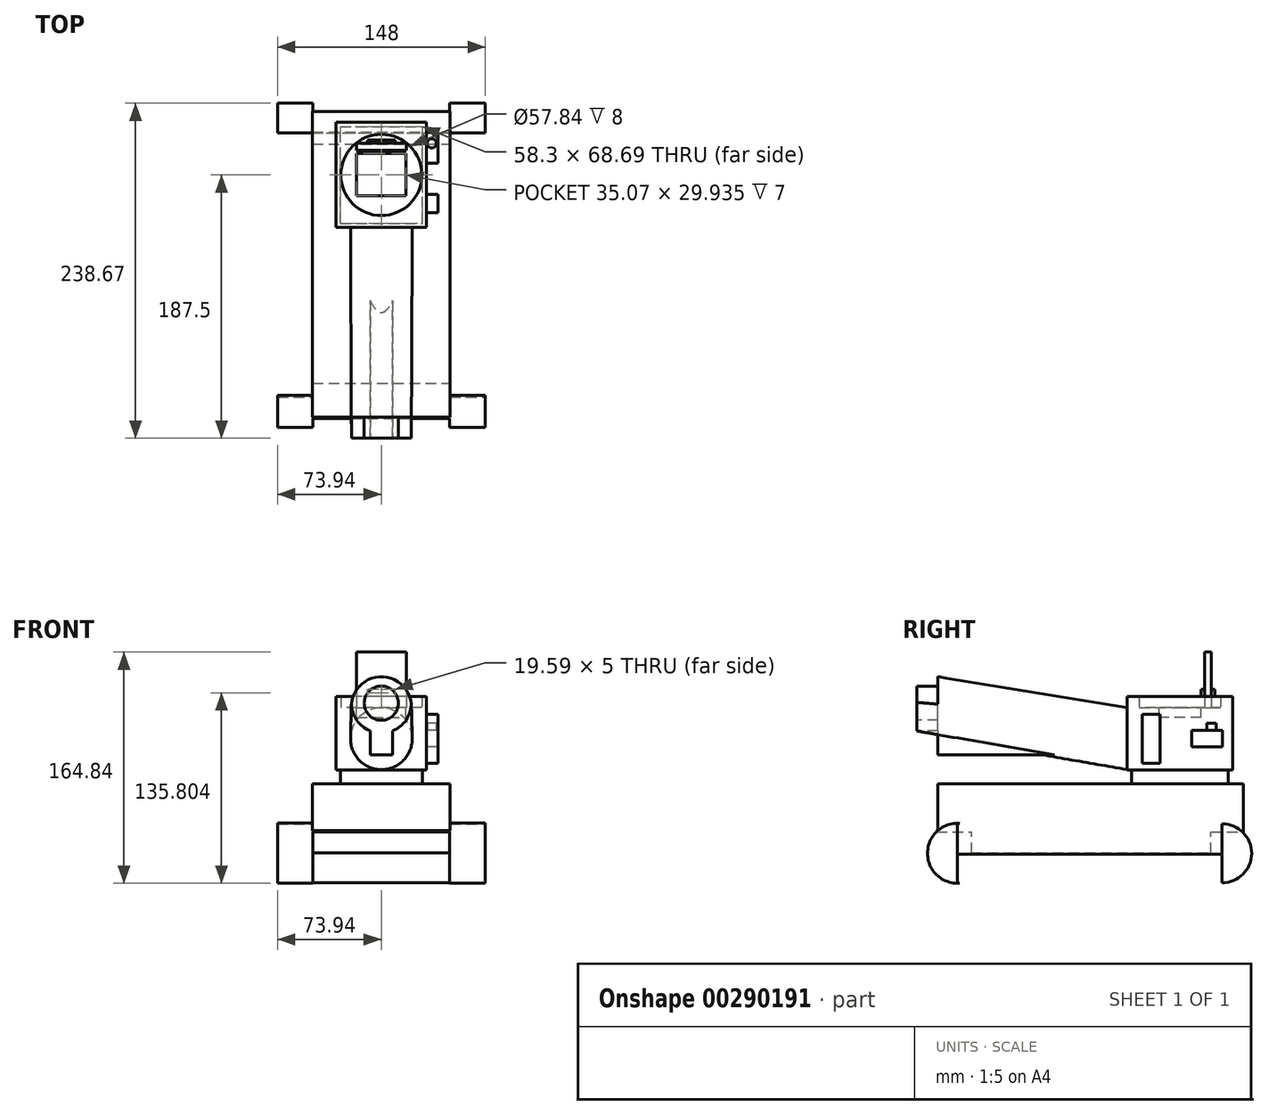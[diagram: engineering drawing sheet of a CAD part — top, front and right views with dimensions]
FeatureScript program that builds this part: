
annotation { "Feature Type Name" : "Feature", "Feature Type Description" : "" }
export const myFeature = defineFeature(function(context is Context, id is Id, definition is map)
    precondition{}
    {
        {
            var Q0;
            Q0=qCreatedBy(makeId("Front.planeOp"),FACE);
            var sketch = newSketch(context, id + "F0", { "sketchPlane" : qUnion([Q0])});
            skCircle(sketch, "E0", {"center": v(0, 0) * mm, "radius": 22 * mm});
            skSolve(sketch);
        }
        {
            var Q0;
            Q0=qCreatedBy(makeId("Front.planeOp"),FACE);
            cPlane(context, id + "F1", {"entities" : qUnion([Q0]), "cplaneType" : CPlaneType.OFFSET, "offset" : 150 * mm, "width" : 150 * mm, "height" : 150 * mm});
        }
        {
            var Q0;
            Q0=qCreatedBy(id+"F1.planeOp",FACE);
            var sketch = newSketch(context, id + "F2", { "sketchPlane" : qUnion([Q0])});
            skCircle(sketch, "E1", {"center": v(0, 25.35) * mm, "radius": 21.35 * mm});
            skSolve(sketch);
        }
        {
            var Q0;
            Q0=makeQuery(id+"F0.imprint","IMPRINT",FACE,{"disambiguationData":[TD([[makeQuery(id+"F0.imprint","IMPRINT",EDGE,{"derivedFrom":sQuery(id+"F0.wireOp",EDGE,"E0")}),1.0]])]});
            var Q1;
            Q1=makeQuery(id+"F2.imprint","IMPRINT",FACE,{"disambiguationData":[TD([[makeQuery(id+"F2.imprint","IMPRINT",EDGE,{"derivedFrom":sQuery(id+"F2.wireOp",EDGE,"E1")}),1.0]])]});
            loft(context, id + "F3", {"sheetProfilesArray" : [{ "sheetProfileEntities" : qUnion([Q0]) }, { "sheetProfileEntities" : qUnion([Q1]) }]});
        }
        {
            var Q0;
            Q0=qCreatedBy(id+"F1.planeOp",FACE);
            var sketch = newSketch(context, id + "F4", { "sketchPlane" : qUnion([Q0])});
            skLineSegment(sketch, "E2.bottom", {"start": v(-7.93, 11.5) * mm, "end": v(7.93, 11.5) * mm});
            skLineSegment(sketch, "E2.top", {"start": v(-7.93, -11.5) * mm, "end": v(7.93, -11.5) * mm});
            skLineSegment(sketch, "E2.left", {"start": v(-7.93, 11.5) * mm, "end": v(-7.93, -11.5) * mm});
            skLineSegment(sketch, "E2.right", {"start": v(7.93, 11.5) * mm, "end": v(7.93, -11.5) * mm});
            skPoint(sketch, "E2.middle", {"position": v(0, 0) * mm});
            skSolve(sketch);
        }
        {
            var Q0;
            Q0=makeQuery(id+"F4.imprint","IMPRINT",FACE,{"disambiguationData":[TD([[makeQuery(id+"F4.imprint","IMPRINT",EDGE,{"derivedFrom":sQuery(id+"F4.wireOp",EDGE,"E2.bottom")}),-1.0]])]});
            extrude(context, id + "F5", {"entities" : qUnion([Q0]), "operationType" : NewBodyOperationType.ADD, "oppositeDirection" : true, "depth" : 120 * mm});
        }
        {
            var Q0;
            Q0=qCreatedBy(makeId("Front.planeOp"),FACE);
            var sketch = newSketch(context, id + "F6", { "sketchPlane" : qUnion([Q0])});
            skLineSegment(sketch, "E3.bottom", {"start": v(32.22, 22.24) * mm, "end": v(-32.22, 22.24) * mm});
            skLineSegment(sketch, "E3.top", {"start": v(32.22, -22.24) * mm, "end": v(-32.22, -22.24) * mm});
            skLineSegment(sketch, "E3.left", {"start": v(32.22, 22.24) * mm, "end": v(32.22, -22.24) * mm});
            skLineSegment(sketch, "E3.right", {"start": v(-32.22, 22.24) * mm, "end": v(-32.22, -22.24) * mm});
            skPoint(sketch, "E3.middle", {"position": v(0, 0) * mm});
            skSolve(sketch);
        }
        {
            var Q0;
            Q0=makeQuery(id+"F6.imprint","IMPRINT",FACE,{"disambiguationData":[TD([[makeQuery(id+"F6.imprint","IMPRINT",EDGE,{"derivedFrom":sQuery(id+"F6.wireOp",EDGE,"E3.bottom")}),1.0]])]});
            extrude(context, id + "F7", {"entities" : qUnion([Q0]), "operationType" : NewBodyOperationType.ADD, "oppositeDirection" : true, "depth" : 75 * mm});
        }
        {
            var Q0;
            Q0=makeQuery(id+"F7.opExtrude","SWEPT_FACE",FACE,{"disambiguationData":[OSD([sQuery(id+"F6.wireOp",EDGE,"E3.bottom")])]});
            var sketch = newSketch(context, id + "F8", { "sketchPlane" : qUnion([Q0])});
            skLineSegment(sketch, "E4", {"start": v(0, 75) * mm, "end": v(0, 0) * mm});
            skLineSegment(sketch, "E5", {"start": v(0, 0) * mm, "end": v(0, 37.5) * mm});
            skCircle(sketch, "E6", {"center": v(0, 37.5) * mm, "radius": 28.92 * mm});
            skSolve(sketch);
        }
        {
            var Q0;
            {var subQ0=sQuery(id+"F8.wireOp",EDGE,"E5");var subQ1=sQuery(id+"F8.wireOp",EDGE,"E4");var subQ2=makeQuery(id+"F8.imprint","INTERSECT",VERTEX,{"derivedFrom":[subQ1,subQ0]});Q0=makeQuery(id+"F8.imprint","IMPRINT",FACE,{"disambiguationData":[TD([[makeQuery(id+"F8.imprint","IMPRINT",EDGE,{"disambiguationData":[TD([[subQ2,1.0]])],"derivedFrom":subQ1}),-1.0]])]});}
            var Q1;
            {var subQ0=sQuery(id+"F8.wireOp",EDGE,"E5");var subQ1=sQuery(id+"F8.wireOp",EDGE,"E4");var subQ2=makeQuery(id+"F8.imprint","INTERSECT",VERTEX,{"derivedFrom":[subQ1,subQ0]});Q1=makeQuery(id+"F8.imprint","IMPRINT",FACE,{"disambiguationData":[TD([[makeQuery(id+"F8.imprint","IMPRINT",EDGE,{"disambiguationData":[TD([[subQ2,1.0]])],"derivedFrom":subQ1}),1.0]])]});}
            extrude(context, id + "F9", {"entities" : qUnion([Q0, Q1]), "operationType" : NewBodyOperationType.ADD, "depth" : 8 * mm});
        }
        {
            var Q0;
            Q0=makeQuery(id+"F7.opExtrude","SWEPT_FACE",FACE,{"disambiguationData":[OSD([sQuery(id+"F6.wireOp",EDGE,"E3.top")])]});
            var sketch = newSketch(context, id + "F10", { "sketchPlane" : qUnion([Q0])});
            skLineSegment(sketch, "E7", {"start": v(0, 0) * mm, "end": v(0, -75) * mm});
            skLineSegment(sketch, "E8", {"start": v(0, -75) * mm, "end": v(0, -37.5) * mm});
            skLineSegment(sketch, "E9.bottom", {"start": v(-29.15, -3.15) * mm, "end": v(29.15, -3.15) * mm});
            skLineSegment(sketch, "E9.top", {"start": v(-29.15, -71.85) * mm, "end": v(29.15, -71.85) * mm});
            skLineSegment(sketch, "E9.left", {"start": v(-29.15, -3.15) * mm, "end": v(-29.15, -71.85) * mm});
            skLineSegment(sketch, "E9.right", {"start": v(29.15, -3.15) * mm, "end": v(29.15, -71.85) * mm});
            skPoint(sketch, "E9.middle", {"position": v(0, -37.5) * mm});
            skSolve(sketch);
        }
        {
            var Q0;
            {var subQ0=sQuery(id+"F10.wireOp",EDGE,"E9.left");Q0=makeQuery(id+"F10.imprint","IMPRINT",FACE,{"disambiguationData":[TD([[makeQuery(id+"F10.imprint","IMPRINT",EDGE,{"derivedFrom":subQ0}),1.0]])]});}
            var Q1;
            {var subQ0=sQuery(id+"F10.wireOp",EDGE,"E9.right");Q1=makeQuery(id+"F10.imprint","IMPRINT",FACE,{"disambiguationData":[TD([[makeQuery(id+"F10.imprint","IMPRINT",EDGE,{"derivedFrom":subQ0}),-1.0]])]});}
            extrude(context, id + "F11", {"entities" : qUnion([Q0, Q1]), "operationType" : NewBodyOperationType.ADD, "depth" : 10 * mm});
        }
        {
            var Q0;
            Q0=makeQuery(id+"F11.opExtrude","CAP_FACE",FACE,{"disambiguationData":[OSD([sQuery(id+"F10.wireOp",EDGE,"E9.bottom"),sQuery(id+"F10.wireOp",EDGE,"E9.top"),sQuery(id+"F10.wireOp",EDGE,"E9.left"),sQuery(id+"F10.wireOp",EDGE,"E9.right")])],"isStart":false});
            var sketch = newSketch(context, id + "F12", { "sketchPlane" : qUnion([Q0])});
            skLineSegment(sketch, "E10.bottom", {"start": v(-77.47, 135.84) * mm, "end": v(77.47, 135.84) * mm});
            skLineSegment(sketch, "E10.top", {"start": v(-77.47, -83.98) * mm, "end": v(77.47, -83.98) * mm});
            skLineSegment(sketch, "E10.left", {"start": v(-77.47, 135.84) * mm, "end": v(-77.47, -83.98) * mm});
            skLineSegment(sketch, "E10.right", {"start": v(77.47, 135.84) * mm, "end": v(77.47, -83.98) * mm});
            skPoint(sketch, "E10.middle", {"position": v(0, 25.93) * mm});
            skSolve(sketch);
        }
        {
            var Q0;
            Q0=makeQuery(id+"F5.boolean.opBoolean","MERGE",FACE,{"derivedFrom":[makeQuery(id+"F3.opLoft","CAP_FACE",FACE,{"disambiguationData":[OSD([makeQuery(id+"F2.imprint","IMPRINT",FACE,{"disambiguationData":[TD([[makeQuery(id+"F2.imprint","IMPRINT",EDGE,{"derivedFrom":sQuery(id+"F2.wireOp",EDGE,"E1")}),1.0]])]})])],"isStart":true}),makeQuery(id+"F5.opExtrude","CAP_FACE",FACE,{"disambiguationData":[OSD([sQuery(id+"F4.wireOp",EDGE,"E2.bottom"),sQuery(id+"F4.wireOp",EDGE,"E2.top"),sQuery(id+"F4.wireOp",EDGE,"E2.left"),sQuery(id+"F4.wireOp",EDGE,"E2.right")])],"isStart":true})]});
            var sketch = newSketch(context, id + "F13", { "sketchPlane" : qUnion([Q0])});
            skLineSegment(sketch, "E11", {"start": v(-21.35, 25.33) * mm, "end": v(21.35, 25.33) * mm});
            skLineSegment(sketch, "E12", {"start": v(21.35, 25.33) * mm, "end": v(0, 25.33) * mm});
            skCircle(sketch, "E13", {"center": v(0, 25.33) * mm, "radius": 12.18 * mm});
            skSolve(sketch);
        }
        {
            var Q0;
            {var subQ0=sQuery(id+"F13.wireOp",EDGE,"E12");var subQ1=sQuery(id+"F13.wireOp",EDGE,"E11");var subQ2=makeQuery(id+"F13.imprint","INTERSECT",VERTEX,{"derivedFrom":[subQ1,subQ0]});Q0=makeQuery(id+"F13.imprint","IMPRINT",FACE,{"disambiguationData":[TD([[makeQuery(id+"F13.imprint","IMPRINT",EDGE,{"disambiguationData":[TD([[subQ2,1.0]])],"derivedFrom":subQ1}),-1.0]])]});}
            var Q1;
            {var subQ0=sQuery(id+"F13.wireOp",EDGE,"E12");var subQ1=sQuery(id+"F13.wireOp",EDGE,"E11");var subQ2=makeQuery(id+"F13.imprint","INTERSECT",VERTEX,{"derivedFrom":[subQ1,subQ0]});Q1=makeQuery(id+"F13.imprint","IMPRINT",FACE,{"disambiguationData":[TD([[makeQuery(id+"F13.imprint","IMPRINT",EDGE,{"disambiguationData":[TD([[subQ2,1.0]])],"derivedFrom":subQ1}),1.0]])]});}
            extrude(context, id + "F14", {"entities" : qUnion([Q0, Q1]), "operationType" : NewBodyOperationType.REMOVE, "oppositeDirection" : true, "depth" : 15 * mm});
        }
        {
            var Q0;
            Q0=makeQuery(id+"F12.imprint","IMPRINT",FACE,{"disambiguationData":[TD([[makeQuery(id+"F12.imprint","IMPRINT",EDGE,{"derivedFrom":makeQuery(id+"F11.opExtrude","CAP_EDGE",EDGE,{"disambiguationData":[OSD([sQuery(id+"F10.wireOp",EDGE,"E9.bottom")])],"isStart":false})}),-1.0]])]});
            var sketch = newSketch(context, id + "F15", { "sketchPlane" : qUnion([Q0])});
            skLineSegment(sketch, "E14.bottom", {"start": v(-49.06, 135.11) * mm, "end": v(49.06, 135.11) * mm});
            skLineSegment(sketch, "E14.top", {"start": v(-49.06, -82.65) * mm, "end": v(49.06, -82.65) * mm});
            skLineSegment(sketch, "E14.left", {"start": v(-49.06, 135.11) * mm, "end": v(-49.06, -82.65) * mm});
            skLineSegment(sketch, "E14.right", {"start": v(49.06, 135.11) * mm, "end": v(49.06, -82.65) * mm});
            skPoint(sketch, "E14.middle", {"position": v(0, 26.23) * mm});
            skSolve(sketch);
        }
        {
            var Q0;
            Q0 = qSketchRegion(id + "F15", true);
            extrude(context, id + "F16", {"entities" : qUnion([Q0]), "operationType" : NewBodyOperationType.ADD, "depth" : 50 * mm});
        }
        {
            var Q0;
            Q0=makeQuery(id+"F16.opExtrude","SWEPT_FACE",FACE,{"disambiguationData":[OSD([sQuery(id+"F15.wireOp",EDGE,"E14.right")])]});
            cPlane(context, id + "F17", {"entities" : qUnion([Q0]), "cplaneType" : CPlaneType.OFFSET, "offset" : 25 * mm, "width" : 150 * mm, "height" : 150 * mm});
        }
        {
            var Q0;
            Q0=qCreatedBy(id+"F17.planeOp",FACE);
            var sketch = newSketch(context, id + "F18", { "sketchPlane" : qUnion([Q0])});
            skLineSegment(sketch, "E15", {"start": v(-135.32, -81.64) * mm, "end": v(81.95, -81.64) * mm});
            skLineSegment(sketch, "E16", {"start": v(81.95, -81.64) * mm, "end": v(-26.69, -81.64) * mm});
            skLineSegment(sketch, "E17", {"start": v(-26.69, -81.64) * mm, "end": v(-135.32, -81.64) * mm});
            skLineSegment(sketch, "E18", {"start": v(-81, -81.64) * mm, "end": v(-26.69, -81.64) * mm});
            skLineSegment(sketch, "E19", {"start": v(27.63, -81.64) * mm, "end": v(-26.69, -81.64) * mm});
            skLineSegment(sketch, "E20", {"start": v(27.63, -81.64) * mm, "end": v(81.95, -81.64) * mm});
            skLineSegment(sketch, "E21.bottom", {"start": v(-120.98, -60.28) * mm, "end": v(67.6, -60.28) * mm});
            skLineSegment(sketch, "E21.top", {"start": v(-120.98, -103) * mm, "end": v(67.6, -103) * mm});
            skLineSegment(sketch, "E21.left", {"start": v(-120.98, -60.28) * mm, "end": v(-120.98, -103) * mm});
            skLineSegment(sketch, "E21.right", {"start": v(67.6, -60.28) * mm, "end": v(67.6, -103) * mm});
            skPoint(sketch, "E21.middle", {"position": v(-26.69, -81.64) * mm});
            skCircle(sketch, "E22", {"center": v(-120.98, -81.64) * mm, "radius": 21.41 * mm});
            skCircle(sketch, "E23", {"center": v(67.6, -81.64) * mm, "radius": 21.06 * mm});
            skSolve(sketch);
        }
        {
            var Q0;
            {var subQ0=sQuery(id+"F18.wireOp",EDGE,"E21.left");var subQ1=sQuery(id+"F18.wireOp",EDGE,"E21.bottom");var subQ2=makeQuery(id+"F18.imprint","INTERSECT",VERTEX,{"derivedFrom":[subQ1,subQ0]});Q0=makeQuery(id+"F18.imprint","IMPRINT",FACE,{"disambiguationData":[TD([[makeQuery(id+"F18.imprint","IMPRINT",EDGE,{"disambiguationData":[TD([[subQ2,-1.0]])],"derivedFrom":subQ1}),1.0]])]});}
            var Q1;
            {var subQ4=sQuery(id+"F18.wireOp",EDGE,"E18");Q1=makeQuery(id+"F18.imprint","IMPRINT",FACE,{"disambiguationData":[TD([[makeQuery(id+"F18.imprint","IMPRINT",EDGE,{"derivedFrom":subQ4}),1.0]])]});}
            var Q2;
            {var subQ8=sQuery(id+"F18.wireOp",EDGE,"E18");Q2=makeQuery(id+"F18.imprint","IMPRINT",FACE,{"disambiguationData":[TD([[makeQuery(id+"F18.imprint","IMPRINT",EDGE,{"derivedFrom":subQ8}),-1.0]])]});}
            var Q3;
            {var subQ0=sQuery(id+"F18.wireOp",EDGE,"E21.left");var subQ1=sQuery(id+"F18.wireOp",EDGE,"E17");var subQ2=makeQuery(id+"F18.imprint","INTERSECT",VERTEX,{"derivedFrom":[subQ1,subQ0]});Q3=makeQuery(id+"F18.imprint","IMPRINT",FACE,{"disambiguationData":[TD([[makeQuery(id+"F18.imprint","IMPRINT",EDGE,{"disambiguationData":[TD([[subQ2,1.0]])],"derivedFrom":subQ1}),1.0]])]});}
            var Q4;
            {var subQ0=sQuery(id+"F18.wireOp",EDGE,"E21.left");var subQ1=sQuery(id+"F18.wireOp",EDGE,"E17");var subQ2=makeQuery(id+"F18.imprint","INTERSECT",VERTEX,{"derivedFrom":[subQ1,subQ0]});Q4=makeQuery(id+"F18.imprint","IMPRINT",FACE,{"disambiguationData":[TD([[makeQuery(id+"F18.imprint","IMPRINT",EDGE,{"disambiguationData":[TD([[subQ2,1.0]])],"derivedFrom":subQ1}),-1.0]])]});}
            var Q5;
            {var subQ0=sQuery(id+"F18.wireOp",EDGE,"E21.right");var subQ1=sQuery(id+"F18.wireOp",EDGE,"E20");var subQ2=makeQuery(id+"F18.imprint","INTERSECT",VERTEX,{"derivedFrom":[subQ1,subQ0]});Q5=makeQuery(id+"F18.imprint","IMPRINT",FACE,{"disambiguationData":[TD([[makeQuery(id+"F18.imprint","IMPRINT",EDGE,{"disambiguationData":[TD([[subQ2,1.0]])],"derivedFrom":subQ1}),1.0]])]});}
            var Q6;
            {var subQ0=sQuery(id+"F18.wireOp",EDGE,"E21.right");var subQ1=makeQuery(id+"F18.imprint","INTERSECT",VERTEX,{"derivedFrom":[sQuery(id+"F18.wireOp",EDGE,"E20"),subQ0]});Q6=makeQuery(id+"F18.imprint","IMPRINT",FACE,{"disambiguationData":[TD([[makeQuery(id+"F18.imprint","IMPRINT",EDGE,{"disambiguationData":[TD([[subQ1,1.0]])],"derivedFrom":subQ0}),1.0]])]});}
            var Q7;
            {var subQ0=sQuery(id+"F18.wireOp",EDGE,"E21.right");var subQ1=sQuery(id+"F18.wireOp",EDGE,"E20");var subQ2=makeQuery(id+"F18.imprint","INTERSECT",VERTEX,{"derivedFrom":[subQ1,subQ0]});Q7=makeQuery(id+"F18.imprint","IMPRINT",FACE,{"disambiguationData":[TD([[makeQuery(id+"F18.imprint","IMPRINT",EDGE,{"disambiguationData":[TD([[subQ2,1.0]])],"derivedFrom":subQ1}),-1.0]])]});}
            extrude(context, id + "F19", {"entities" : qUnion([Q0, Q1, Q2, Q3, Q4, Q5, Q6, Q7]), "operationType" : NewBodyOperationType.ADD, "oppositeDirection" : true, "depth" : 148 * mm});
        }
        {
            var Q0;
            Q0=qCreatedBy(makeId("Front.planeOp"),FACE);
            cPlane(context, id + "F20", {"entities" : qUnion([Q0]), "cplaneType" : CPlaneType.OFFSET, "offset" : 60 * mm, "oppositeDirection" : true, "width" : 150 * mm, "height" : 150 * mm});
        }
        {
            var Q0;
            Q0=qCreatedBy(id+"F20.planeOp",FACE);
            var sketch = newSketch(context, id + "F21", { "sketchPlane" : qUnion([Q0])});
            skLineSegment(sketch, "E24.bottom", {"start": v(17.7, 61.78) * mm, "end": v(-17.7, 61.78) * mm});
            skLineSegment(sketch, "E24.top", {"start": v(17.7, -16.34) * mm, "end": v(-17.7, -16.34) * mm});
            skLineSegment(sketch, "E24.left", {"start": v(17.7, 61.78) * mm, "end": v(17.7, -16.34) * mm});
            skLineSegment(sketch, "E24.right", {"start": v(-17.7, 61.78) * mm, "end": v(-17.7, -16.34) * mm});
            skPoint(sketch, "E24.middle", {"position": v(0, 22.72) * mm});
            skSolve(sketch);
        }
        {
            var Q0;
            Q0=makeQuery(id+"F21.imprint","IMPRINT",FACE,{"disambiguationData":[TD([[makeQuery(id+"F21.imprint","IMPRINT",EDGE,{"derivedFrom":sQuery(id+"F21.wireOp",EDGE,"E24.bottom")}),1.0]])]});
            extrude(context, id + "F22", {"entities" : qUnion([Q0]), "operationType" : NewBodyOperationType.ADD, "depth" : 5 * mm});
        }
        {
            var Q0;
            Q0=makeQuery(id+"F9.opExtrude","CAP_FACE",FACE,{"disambiguationData":[OSD([sQuery(id+"F8.wireOp",EDGE,"E6")])],"isStart":false});
            var sketch = newSketch(context, id + "F23", { "sketchPlane" : qUnion([Q0])});
            skLineSegment(sketch, "E25", {"start": v(0, 60) * mm, "end": v(0, 55) * mm});
            skLineSegment(sketch, "E26", {"start": v(0, 55) * mm, "end": v(0, 57.5) * mm});
            skLineSegment(sketch, "E27.bottom", {"start": v(-9.8, 62.3) * mm, "end": v(9.8, 62.3) * mm});
            skLineSegment(sketch, "E27.top", {"start": v(-9.8, 52.7) * mm, "end": v(9.8, 52.7) * mm});
            skLineSegment(sketch, "E27.left", {"start": v(-9.8, 62.3) * mm, "end": v(-9.8, 52.7) * mm});
            skLineSegment(sketch, "E27.right", {"start": v(9.8, 62.3) * mm, "end": v(9.8, 52.7) * mm});
            skPoint(sketch, "E27.middle", {"position": v(0, 57.5) * mm});
            skSolve(sketch);
        }
        {
            var Q0;
            {var subQ1=sQuery(id+"F23.wireOp",EDGE,"E27.bottom");Q0=makeQuery(id+"F23.imprint","IMPRINT",FACE,{"disambiguationData":[TD([[makeQuery(id+"F23.imprint","IMPRINT",EDGE,{"derivedFrom":subQ1}),-1.0]])]});}
            var Q1;
            {var subQ5=sQuery(id+"F23.wireOp",EDGE,"E27.top");Q1=makeQuery(id+"F23.imprint","IMPRINT",FACE,{"disambiguationData":[TD([[makeQuery(id+"F23.imprint","IMPRINT",EDGE,{"derivedFrom":subQ5}),1.0]])]});}
            extrude(context, id + "F24", {"entities" : qUnion([Q0, Q1]), "operationType" : NewBodyOperationType.ADD, "depth" : 5 * mm});
        }
        {
            var Q0;
            Q0=makeQuery(id+"F9.opExtrude","CAP_FACE",FACE,{"disambiguationData":[OSD([sQuery(id+"F8.wireOp",EDGE,"E6")])],"isStart":false});
            var sketch = newSketch(context, id + "F25", { "sketchPlane" : qUnion([Q0])});
            skLineSegment(sketch, "E28.bottom", {"start": v(-17.7, 52.7) * mm, "end": v(17.37, 52.7) * mm});
            skLineSegment(sketch, "E28.top", {"start": v(-17.7, 22.77) * mm, "end": v(17.37, 22.77) * mm});
            skLineSegment(sketch, "E28.left", {"start": v(-17.7, 52.7) * mm, "end": v(-17.7, 22.77) * mm});
            skLineSegment(sketch, "E28.right", {"start": v(17.37, 52.7) * mm, "end": v(17.37, 22.77) * mm});
            skSolve(sketch);
        }
        {
            var Q0;
            Q0=makeQuery(id+"F25.imprint","IMPRINT",FACE,{"disambiguationData":[TD([[makeQuery(id+"F25.imprint","IMPRINT",EDGE,{"derivedFrom":sQuery(id+"F25.wireOp",EDGE,"E28.top")}),1.0]])]});
            extrude(context, id + "F26", {"entities" : qUnion([Q0]), "operationType" : NewBodyOperationType.REMOVE, "oppositeDirection" : true, "depth" : 15 * mm});
        }
        {
            var Q0;
            Q0=qCreatedBy(id+"F20.planeOp",FACE);
            cPlane(context, id + "F27", {"entities" : qUnion([Q0]), "cplaneType" : CPlaneType.OFFSET, "offset" : 30 * mm, "oppositeDirection" : true, "width" : 150 * mm, "height" : 150 * mm});
        }
        {
            var Q0;
            Q0=qCreatedBy(id+"F27.planeOp",FACE);
            var sketch = newSketch(context, id + "F28", { "sketchPlane" : qUnion([Q0])});
            skLineSegment(sketch, "E29", {"start": v(48.67, -66.39) * mm, "end": v(-48.98, -66.39) * mm});
            skLineSegment(sketch, "E30", {"start": v(-48.98, -66.39) * mm, "end": v(-48.98, -102.7) * mm});
            skLineSegment(sketch, "E31", {"start": v(-48.98, -102.7) * mm, "end": v(48.67, -66.39) * mm});
            skLineSegment(sketch, "E32", {"start": v(48.67, -66.39) * mm, "end": v(48.67, -102.7) * mm});
            skLineSegment(sketch, "E33", {"start": v(48.67, -102.7) * mm, "end": v(-48.98, -102.7) * mm});
            skSolve(sketch);
        }
        {
            var Q0;
            Q0=makeQuery(id+"F28.imprint","IMPRINT",FACE,{"disambiguationData":[TD([[makeQuery(id+"F28.imprint","IMPRINT",EDGE,{"derivedFrom":sQuery(id+"F28.wireOp",EDGE,"E31")}),-1.0]])]});
            var Q1;
            Q1=makeQuery(id+"F28.imprint","IMPRINT",FACE,{"disambiguationData":[TD([[makeQuery(id+"F28.imprint","IMPRINT",EDGE,{"derivedFrom":sQuery(id+"F28.wireOp",EDGE,"E29")}),1.0]])]});
            extrude(context, id + "F29", {"entities" : qUnion([Q0, Q1]), "operationType" : NewBodyOperationType.REMOVE, "depth" : 250 * mm});
        }
        {
            var Q0;
            Q0=makeQuery(id+"F19.opExtrude","SWEPT_FACE",FACE,{"disambiguationData":[OSD([sQuery(id+"F18.wireOp",EDGE,"E21.top")])]});
            var sketch = newSketch(context, id + "F30", { "sketchPlane" : qUnion([Q0])});
            skLineSegment(sketch, "E34", {"start": v(-49.07, 125.1) * mm, "end": v(-49.07, -67.6) * mm});
            skLineSegment(sketch, "E35", {"start": v(-49.07, -67.6) * mm, "end": v(-49.07, -75.33) * mm});
            skLineSegment(sketch, "E36", {"start": v(-49.07, -75.33) * mm, "end": v(48.05, -75.33) * mm});
            skLineSegment(sketch, "E37", {"start": v(48.05, -75.33) * mm, "end": v(48.05, -67.6) * mm});
            skLineSegment(sketch, "E38", {"start": v(48.05, -67.6) * mm, "end": v(48.05, 125.06) * mm});
            skLineSegment(sketch, "E39", {"start": v(48.05, 125.06) * mm, "end": v(-49.07, 125.1) * mm});
            skSolve(sketch);
        }
        {
            var Q0;
            {var subQ0=sQuery(id+"F30.wireOp",EDGE,"E34");var subQ1=sQuery(id+"F18.wireOp",EDGE,"E21.top");var subQ4=makeQuery(id+"F19.opExtrude","SWEPT_EDGE",EDGE,{"disambiguationData":[OSD([subQ1,sQuery(id+"F18.wireOp",EDGE,"E22")])]});var subQ5=makeQuery(id+"F30.imprint","INTERSECT",VERTEX,{"derivedFrom":[subQ4,subQ0]});Q0=makeQuery(id+"F30.imprint","IMPRINT",FACE,{"disambiguationData":[TD([[makeQuery(id+"F30.imprint","IMPRINT",EDGE,{"disambiguationData":[TD([[subQ5,-1.0]])],"derivedFrom":subQ0}),1.0]])]});}
            var Q1;
            {var subQ0=sQuery(id+"F30.wireOp",EDGE,"E39");Q1=makeQuery(id+"F30.imprint","IMPRINT",FACE,{"disambiguationData":[TD([[makeQuery(id+"F30.imprint","IMPRINT",EDGE,{"derivedFrom":subQ0}),1.0]])]});}
            var Q2;
            {var subQ0=sQuery(id+"F30.wireOp",EDGE,"E35");Q2=makeQuery(id+"F30.imprint","IMPRINT",FACE,{"disambiguationData":[TD([[makeQuery(id+"F30.imprint","IMPRINT",EDGE,{"derivedFrom":subQ0}),1.0]])]});}
            extrude(context, id + "F31", {"entities" : qUnion([Q0, Q1, Q2]), "operationType" : NewBodyOperationType.REMOVE, "oppositeDirection" : true, "depth" : 25 * mm});
        }
        {
            var Q0;
            Q0=makeQuery(id+"F29.boolean.opBoolean","COPY",FACE,{"derivedFrom":makeQuery(id+"F29.opExtrude","SWEPT_FACE",FACE,{"disambiguationData":[OSD([sQuery(id+"F28.wireOp",EDGE,"E29")])]})});
            var sketch = newSketch(context, id + "F32", { "sketchPlane" : qUnion([Q0])});
            skLineSegment(sketch, "E40.bottom", {"start": v(-48.98, 126.82) * mm, "end": v(48.98, 126.82) * mm});
            skLineSegment(sketch, "E40.top", {"start": v(-48.98, 37.5) * mm, "end": v(48.98, 37.5) * mm});
            skLineSegment(sketch, "E40.left", {"start": v(-48.98, 126.82) * mm, "end": v(-48.98, 37.5) * mm});
            skLineSegment(sketch, "E40.right", {"start": v(48.98, 126.82) * mm, "end": v(48.98, 37.5) * mm});
            skPoint(sketch, "E40.middle", {"position": v(0, 82.16) * mm});
            skSolve(sketch);
        }
        {
            var Q0;
            {var subQ0=sQuery(id+"F32.wireOp",EDGE,"E40.left");Q0=makeQuery(id+"F32.imprint","IMPRINT",FACE,{"disambiguationData":[TD([[makeQuery(id+"F32.imprint","IMPRINT",EDGE,{"derivedFrom":subQ0}),1.0]])]});}
            extrude(context, id + "F33", {"entities" : qUnion([Q0]), "operationType" : NewBodyOperationType.REMOVE, "depth" : 100 * mm});
        }
        {
            var Q0;
            Q0=makeQuery(id+"F29.boolean.opBoolean","COPY",FACE,{"derivedFrom":makeQuery(id+"F29.opExtrude","SWEPT_FACE",FACE,{"disambiguationData":[OSD([sQuery(id+"F28.wireOp",EDGE,"E29")])]})});
            var sketch = newSketch(context, id + "F34", { "sketchPlane" : qUnion([Q0])});
            skLineSegment(sketch, "E41.bottom", {"start": v(-48.98, 59.64) * mm, "end": v(48.98, 59.64) * mm});
            skLineSegment(sketch, "E41.top", {"start": v(-48.98, -59.64) * mm, "end": v(48.98, -59.64) * mm});
            skLineSegment(sketch, "E41.left", {"start": v(-48.98, 59.64) * mm, "end": v(-48.98, -59.64) * mm});
            skLineSegment(sketch, "E41.right", {"start": v(48.98, 59.64) * mm, "end": v(48.98, -59.64) * mm});
            skPoint(sketch, "E41.middle", {"position": v(0, 0) * mm});
            skLineSegment(sketch, "E42.bottom", {"start": v(-48.98, 110.98) * mm, "end": v(48.98, 110.98) * mm});
            skLineSegment(sketch, "E42.top", {"start": v(-48.98, 72.3) * mm, "end": v(48.98, 72.3) * mm});
            skLineSegment(sketch, "E42.left", {"start": v(-48.98, 110.98) * mm, "end": v(-48.98, 72.3) * mm});
            skLineSegment(sketch, "E42.right", {"start": v(48.98, 110.98) * mm, "end": v(48.98, 72.3) * mm});
            skPoint(sketch, "E42.middle", {"position": v(0, 91.64) * mm});
            skLineSegment(sketch, "E43.bottom", {"start": v(-48.98, 80.21) * mm, "end": v(48.98, 80.21) * mm});
            skLineSegment(sketch, "E43.top", {"start": v(-48.98, 49.43) * mm, "end": v(48.98, 49.43) * mm});
            skLineSegment(sketch, "E43.left", {"start": v(-48.98, 80.21) * mm, "end": v(-48.98, 49.43) * mm});
            skLineSegment(sketch, "E43.right", {"start": v(48.98, 80.21) * mm, "end": v(48.98, 49.43) * mm});
            skPoint(sketch, "E43.middle", {"position": v(0, 64.82) * mm});
            skSolve(sketch);
        }
        {
            var Q0;
            {var subQ0=sQuery(id+"F34.wireOp",EDGE,"E42.left");Q0=makeQuery(id+"F34.imprint","IMPRINT",FACE,{"disambiguationData":[TD([[makeQuery(id+"F34.imprint","IMPRINT",EDGE,{"derivedFrom":subQ0}),1.0]])]});}
            var Q1;
            {var subQ0=sQuery(id+"F34.wireOp",EDGE,"E43.left");var subQ1=sQuery(id+"F34.wireOp",EDGE,"E42.top");var subQ2=makeQuery(id+"F34.imprint","INTERSECT",VERTEX,{"derivedFrom":[subQ1,subQ0]});Q1=makeQuery(id+"F34.imprint","IMPRINT",FACE,{"disambiguationData":[TD([[makeQuery(id+"F34.imprint","IMPRINT",EDGE,{"disambiguationData":[TD([[subQ2,1.0]])],"derivedFrom":subQ0}),1.0]])]});}
            var Q2;
            {var subQ0=sQuery(id+"F34.wireOp",EDGE,"E43.left");var subQ1=sQuery(id+"F34.wireOp",EDGE,"E41.bottom");var subQ2=makeQuery(id+"F34.imprint","INTERSECT",VERTEX,{"derivedFrom":[subQ1,subQ0]});Q2=makeQuery(id+"F34.imprint","IMPRINT",FACE,{"disambiguationData":[TD([[makeQuery(id+"F34.imprint","IMPRINT",EDGE,{"disambiguationData":[TD([[subQ2,1.0]])],"derivedFrom":subQ0}),1.0]])]});}
            var Q3;
            {var subQ0=sQuery(id+"F34.wireOp",EDGE,"E43.left");var subQ1=sQuery(id+"F34.wireOp",EDGE,"E41.bottom");var subQ2=makeQuery(id+"F34.imprint","INTERSECT",VERTEX,{"derivedFrom":[subQ1,subQ0]});Q3=makeQuery(id+"F34.imprint","IMPRINT",FACE,{"disambiguationData":[TD([[makeQuery(id+"F34.imprint","IMPRINT",EDGE,{"disambiguationData":[TD([[subQ2,-1.0]])],"derivedFrom":subQ0}),1.0]])]});}
            var Q4;
            {var subQ0=sQuery(id+"F34.wireOp",EDGE,"E41.left");Q4=makeQuery(id+"F34.imprint","IMPRINT",FACE,{"disambiguationData":[TD([[makeQuery(id+"F34.imprint","IMPRINT",EDGE,{"derivedFrom":subQ0}),1.0]])]});}
            extrude(context, id + "F35", {"entities" : qUnion([Q0, Q1, Q2, Q3, Q4]), "operationType" : NewBodyOperationType.ADD, "depth" : 15 * mm});
        }
        {
            var Q0;
            Q0=makeQuery(id+"F7.opExtrude","SWEPT_FACE",FACE,{"disambiguationData":[OSD([sQuery(id+"F6.wireOp",EDGE,"E3.left")])]});
            var sketch = newSketch(context, id + "F36", { "sketchPlane" : qUnion([Q0])});
            skLineSegment(sketch, "E44.bottom", {"start": v(10.7, 17.53) * mm, "end": v(23.5, 17.53) * mm});
            skLineSegment(sketch, "E44.top", {"start": v(10.7, -17.53) * mm, "end": v(23.5, -17.53) * mm});
            skLineSegment(sketch, "E44.left", {"start": v(10.7, 17.53) * mm, "end": v(10.7, -17.53) * mm});
            skLineSegment(sketch, "E44.right", {"start": v(23.5, 17.53) * mm, "end": v(23.5, -17.53) * mm});
            skPoint(sketch, "E44.middle", {"position": v(17.1, 0) * mm});
            skLineSegment(sketch, "E45.bottom", {"start": v(45.79, 5.93) * mm, "end": v(67.76, 5.93) * mm});
            skLineSegment(sketch, "E45.top", {"start": v(45.79, -5.93) * mm, "end": v(67.76, -5.93) * mm});
            skLineSegment(sketch, "E45.left", {"start": v(45.79, 5.93) * mm, "end": v(45.79, -5.93) * mm});
            skLineSegment(sketch, "E45.right", {"start": v(67.76, 5.93) * mm, "end": v(67.76, -5.93) * mm});
            skPoint(sketch, "E45.middle", {"position": v(56.77, 0) * mm});
            skSolve(sketch);
        }
        {
            var Q0;
            Q0=makeQuery(id+"F36.imprint","IMPRINT",FACE,{"disambiguationData":[TD([[makeQuery(id+"F36.imprint","IMPRINT",EDGE,{"derivedFrom":sQuery(id+"F36.wireOp",EDGE,"E44.bottom")}),-1.0]])]});
            var Q1;
            Q1=makeQuery(id+"F36.imprint","IMPRINT",FACE,{"disambiguationData":[TD([[makeQuery(id+"F36.imprint","IMPRINT",EDGE,{"derivedFrom":sQuery(id+"F36.wireOp",EDGE,"E45.bottom")}),-1.0]])]});
            extrude(context, id + "F37", {"entities" : qUnion([Q0, Q1]), "operationType" : NewBodyOperationType.ADD, "depth" : 8 * mm});
        }
        {
            var Q0;
            Q0=makeQuery(id+"F37.opExtrude","SWEPT_FACE",FACE,{"disambiguationData":[OSD([sQuery(id+"F36.wireOp",EDGE,"E45.bottom")])]});
            var sketch = newSketch(context, id + "F38", { "sketchPlane" : qUnion([Q0])});
            skCircle(sketch, "E46", {"center": v(35.93, 60.05) * mm, "radius": 3.28 * mm});
            skSolve(sketch);
        }
        {
            var Q0;
            Q0=makeQuery(id+"F38.imprint","IMPRINT",FACE,{"disambiguationData":[TD([[makeQuery(id+"F38.imprint","IMPRINT",EDGE,{"derivedFrom":sQuery(id+"F38.wireOp",EDGE,"E46")}),1.0]])]});
            extrude(context, id + "F39", {"entities" : qUnion([Q0]), "operationType" : NewBodyOperationType.ADD, "depth" : 5 * mm});
        }
        {
            var Q0;
            Q0=makeQuery(id+"F39.opExtrude","CAP_FACE",FACE,{"disambiguationData":[OSD([sQuery(id+"F38.wireOp",EDGE,"E46")])],"isStart":false});
            var sketch = newSketch(context, id + "F40", { "sketchPlane" : qUnion([Q0])});
            skCircle(sketch, "E47", {"center": v(35.93, 60.05) * mm, "radius": 0.6 * mm});
            skSolve(sketch);
        }
        {
            var Q0;
            Q0=sQuery(id+"F40.wireOp",EDGE,"E47");
            extrude(context, id + "F41", {"bodyType" : ToolBodyType.SURFACE, "surfaceEntities" : qUnion([Q0]), "depth" : 75 * mm});
        }
    });
